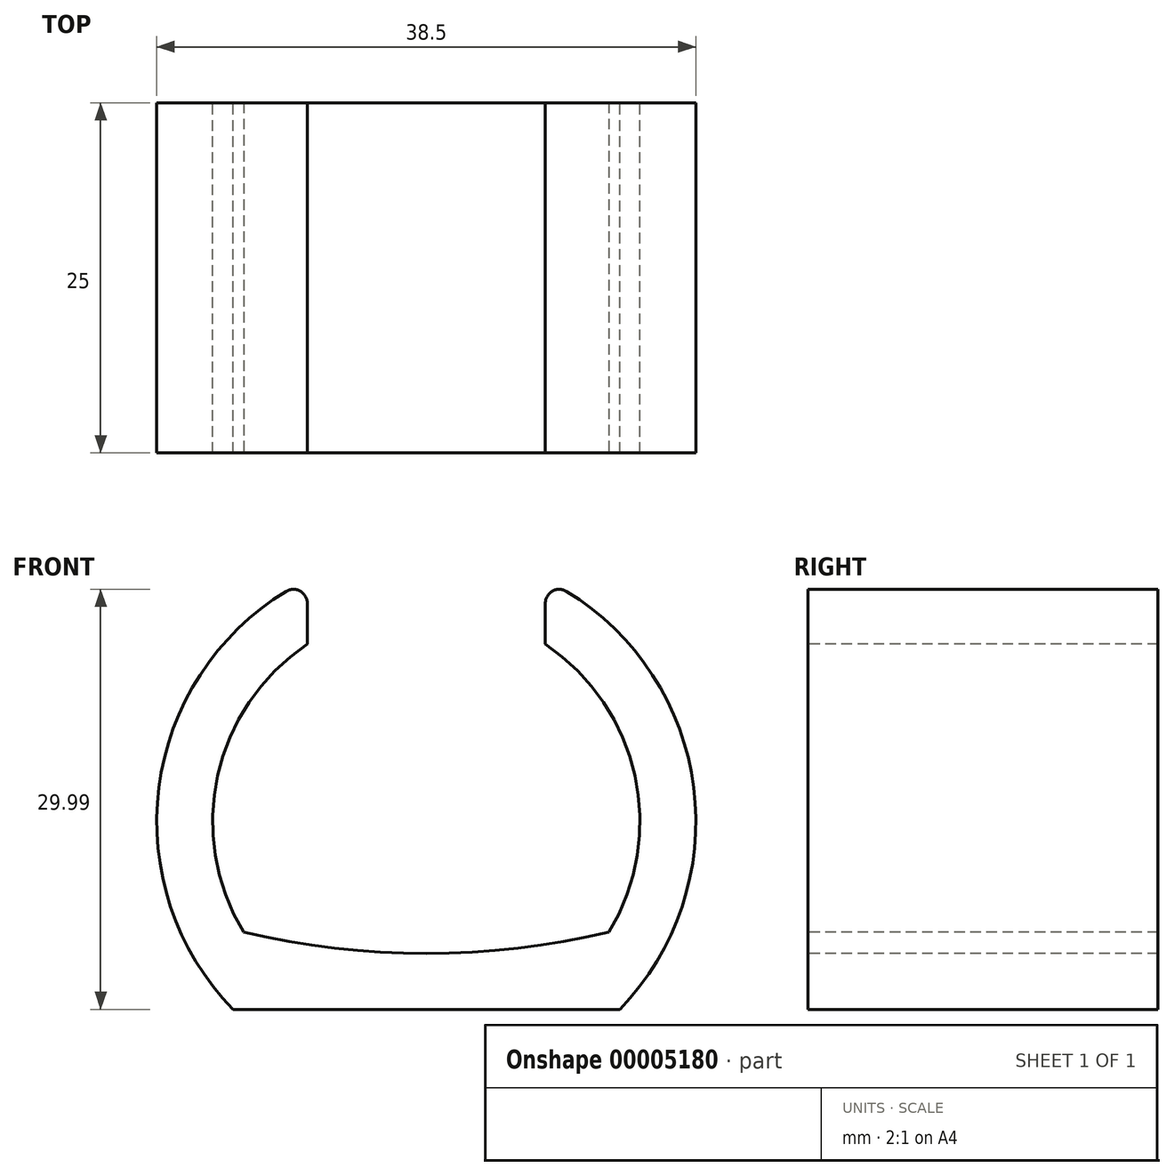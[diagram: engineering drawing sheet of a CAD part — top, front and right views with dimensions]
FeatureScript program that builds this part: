
annotation { "Feature Type Name" : "Feature", "Feature Type Description" : "" }
export const myFeature = defineFeature(function(context is Context, id is Id, definition is map)
    precondition{}
    {
        {
            var Q0;
            Q0=qCreatedBy(makeId("Front.planeOp"),FACE);
            var sketch = newSketch(context, id + "F0", { "sketchPlane" : qUnion([Q0])});
            skArc(sketch, "E0", {"start": v(12, -9.41) * mm, "mid": v(0, 15.25) * mm, "end": v(-12, -9.41) * mm});
            skLineSegment(sketch, "E1", {"start": v(-12, -9.41) * mm, "end": v(12, -9.41) * mm});
            skArc(sketch, "E2.0", {"start": v(13.8, -13.41) * mm, "mid": v(0, 19.25) * mm, "end": v(-13.8, -13.41) * mm});
            skLineSegment(sketch, "E2.1", {"start": v(-13.8, -13.41) * mm, "end": v(13.8, -13.41) * mm});
            skLineSegment(sketch, "E3", {"start": v(0, 0) * mm, "end": v(0, -9.41) * mm, "construction": true});
            skSolve(sketch);
        }
        {
            var Q0;
            Q0 = qSketchRegion(id + "F0", true);
            extrude(context, id + "F1", {"entities" : qUnion([Q0]), "depth" : 25 * mm});
        }
        {
            var Q0;
            Q0=makeQuery(id+"F1.opExtrude","CAP_FACE",FACE,{"disambiguationData":[OSD([sQuery(id+"F0.wireOp",EDGE,"E0"),sQuery(id+"F0.wireOp",EDGE,"E1"),sQuery(id+"F0.wireOp",EDGE,"E2.0"),sQuery(id+"F0.wireOp",EDGE,"E2.1")])],"isStart":false});
            var sketch = newSketch(context, id + "F2", { "sketchPlane" : qUnion([Q0])});
            skLineSegment(sketch, "E4.bottom", {"start": v(-8.5, 19.25) * mm, "end": v(8.5, 19.25) * mm});
            skLineSegment(sketch, "E4.top", {"start": v(-8.5, 12.66) * mm, "end": v(8.5, 12.66) * mm});
            skLineSegment(sketch, "E4.left", {"start": v(-8.5, 19.25) * mm, "end": v(-8.5, 12.66) * mm});
            skLineSegment(sketch, "E4.right", {"start": v(8.5, 19.25) * mm, "end": v(8.5, 12.66) * mm});
            skLineSegment(sketch, "E5", {"start": v(0, 0) * mm, "end": v(0, -13.41) * mm, "construction": true});
            skSolve(sketch);
        }
        {
            var Q0;
            Q0 = qSketchRegion(id + "F2", true);
            extrude(context, id + "F3", {"entities" : qUnion([Q0]), "operationType" : NewBodyOperationType.REMOVE, "endBound" : BoundingType.THROUGH_ALL, "oppositeDirection" : true, "depth" : 25 * mm});
        }
        {
            var Q0;
            Q0=makeQuery(id+"F3.boolean.opBoolean","INTERSECT",EDGE,{"derivedFrom":[makeQuery(id+"F1.opExtrude","SWEPT_FACE",FACE,{"disambiguationData":[OSD([sQuery(id+"F0.wireOp",EDGE,"E2.0")])]}),makeQuery(id+"F3.opExtrude","SWEPT_FACE",FACE,{"disambiguationData":[OSD([sQuery(id+"F2.wireOp",EDGE,"E4.left")])]})]});
            var Q1;
            Q1=makeQuery(id+"F3.boolean.opBoolean","COPY",EDGE,{"derivedFrom":makeQuery(id+"F3.opExtrude","SWEPT_EDGE",EDGE,{"disambiguationData":[OSD([sQuery(id+"F0.wireOp",EDGE,"E0"),sQuery(id+"F2.wireOp",EDGE,"E4.top"),sQuery(id+"F2.wireOp",EDGE,"E4.left")])]})});
            var Q2;
            Q2=makeQuery(id+"F3.boolean.opBoolean","INTERSECT",EDGE,{"derivedFrom":[makeQuery(id+"F1.opExtrude","SWEPT_FACE",FACE,{"disambiguationData":[OSD([sQuery(id+"F0.wireOp",EDGE,"E2.0")])]}),makeQuery(id+"F3.opExtrude","SWEPT_FACE",FACE,{"disambiguationData":[OSD([sQuery(id+"F2.wireOp",EDGE,"E4.right")])]})]});
            var Q3;
            Q3=makeQuery(id+"F3.boolean.opBoolean","COPY",EDGE,{"derivedFrom":makeQuery(id+"F3.opExtrude","SWEPT_EDGE",EDGE,{"disambiguationData":[OSD([sQuery(id+"F0.wireOp",EDGE,"E0"),sQuery(id+"F2.wireOp",EDGE,"E4.top"),sQuery(id+"F2.wireOp",EDGE,"E4.right")])]})});
            fillet(context, id + "F4", {"entities" : qUnion([Q0, Q1, Q2, Q3]), "radius" : 1 * mm, "tangentPropagation" : true, "allowEdgeOverflow" : false});
        }
        {
            var Q0;
            Q0=makeQuery(id+"F1.opExtrude","CAP_FACE",FACE,{"disambiguationData":[OSD([sQuery(id+"F0.wireOp",EDGE,"E0"),sQuery(id+"F0.wireOp",EDGE,"E1"),sQuery(id+"F0.wireOp",EDGE,"E2.0"),sQuery(id+"F0.wireOp",EDGE,"E2.1")])],"isStart":false});
            var sketch = newSketch(context, id + "F5", { "sketchPlane" : qUnion([Q0])});
            skArc(sketch, "E6", {"start": v(-13.04, -7.91) * mm, "mid": v(0, -9.41) * mm, "end": v(13.04, -7.91) * mm});
            skArc(sketch, "E7.0", {"start": v(-13.04, -7.91) * mm, "mid": v(-12.54, -8.68) * mm, "end": v(-12, -9.41) * mm});
            skArc(sketch, "E7.1", {"start": v(12, -9.41) * mm, "mid": v(12.54, -8.68) * mm, "end": v(13.04, -7.91) * mm});
            skLineSegment(sketch, "E7.2", {"start": v(-12, -9.41) * mm, "end": v(12, -9.41) * mm});
            skPoint(sketch, "E8.orphan", {"position": v(-8.92, 12.37) * mm});
            skPoint(sketch, "E9.orphan", {"position": v(8.92, 12.37) * mm});
            skSolve(sketch);
        }
        {
            var Q0;
            Q0 = qSketchRegion(id + "F5", true);
            var Q1;
            Q1=makeQuery(id+"F1.opExtrude","CAP_FACE",FACE,{"disambiguationData":[OSD([sQuery(id+"F0.wireOp",EDGE,"E0"),sQuery(id+"F0.wireOp",EDGE,"E1"),sQuery(id+"F0.wireOp",EDGE,"E2.0"),sQuery(id+"F0.wireOp",EDGE,"E2.1")])],"isStart":true});
            extrude(context, id + "F6", {"entities" : qUnion([Q0]), "operationType" : NewBodyOperationType.ADD, "endBound" : BoundingType.UP_TO_SURFACE, "oppositeDirection" : true, "endBoundEntityFace" : qUnion([Q1]), "depth" : 25 * mm});
        }
    });
